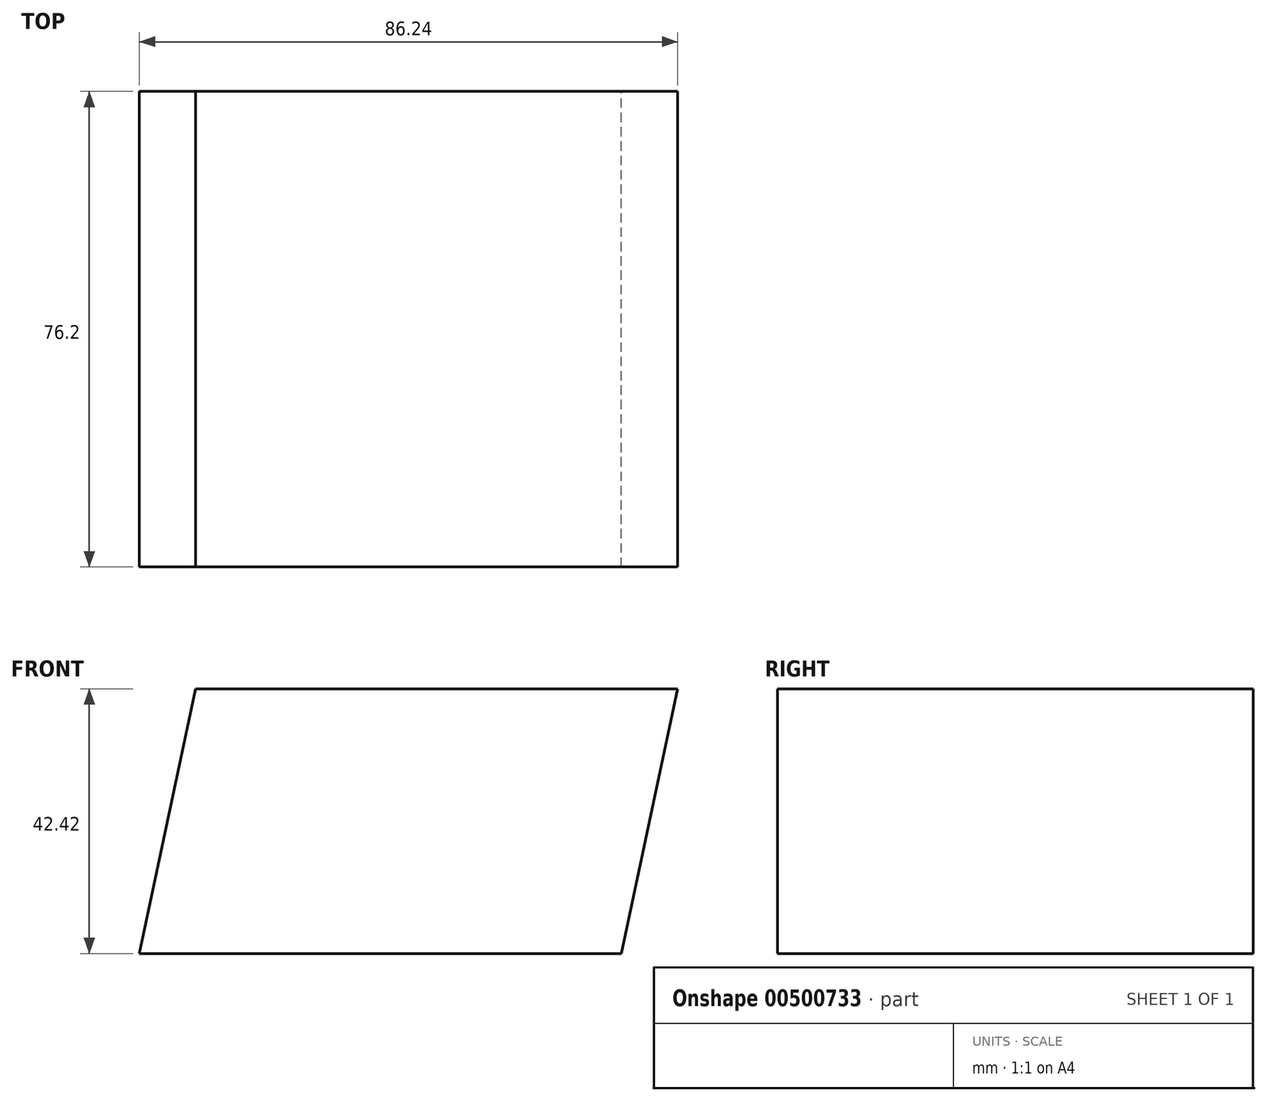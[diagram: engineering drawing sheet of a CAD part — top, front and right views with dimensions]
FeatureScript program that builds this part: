
annotation { "Feature Type Name" : "Feature", "Feature Type Description" : "" }
export const myFeature = defineFeature(function(context is Context, id is Id, definition is map)
    precondition{}
    {
        {
            var Q0;
            Q0=qCreatedBy(makeId("Front.planeOp"),FACE);
            var sketch = newSketch(context, id + "F0", { "sketchPlane" : qUnion([Q0])});
            skLineSegment(sketch, "E0.bottom", {"start": v(-55.74, 56.71) * mm, "end": v(21.48, 56.71) * mm});
            skLineSegment(sketch, "E0.top", {"start": v(-64.76, 14.3) * mm, "end": v(12.46, 14.3) * mm});
            skLineSegment(sketch, "E1", {"start": v(12.46, 14.3) * mm, "end": v(21.48, 56.71) * mm});
            skLineSegment(sketch, "E2", {"start": v(-55.74, 56.71) * mm, "end": v(-64.76, 14.3) * mm});
            skLineSegment(sketch, "E3", {"start": v(-55.74, 56.71) * mm, "end": v(-55.74, 14.3) * mm});
            skSolve(sketch);
        }
        {
            var Q0;
            {var subQ0=sQuery(id+"F0.wireOp",EDGE,"E2");Q0=makeQuery(id+"F0.imprint","IMPRINT",FACE,{"disambiguationData":[TD([[makeQuery(id+"F0.imprint","IMPRINT",EDGE,{"derivedFrom":subQ0}),1.0]])]});}
            var Q1;
            Q1=makeQuery(id+"F0.imprint","IMPRINT",FACE,{"disambiguationData":[TD([[makeQuery(id+"F0.imprint","IMPRINT",EDGE,{"derivedFrom":sQuery(id+"F0.wireOp",EDGE,"E0.bottom")}),-1.0]])]});
            extrude(context, id + "F1", {"entities" : qUnion([Q0, Q1]), "depth" : 76.2 * mm});
        }
    });
